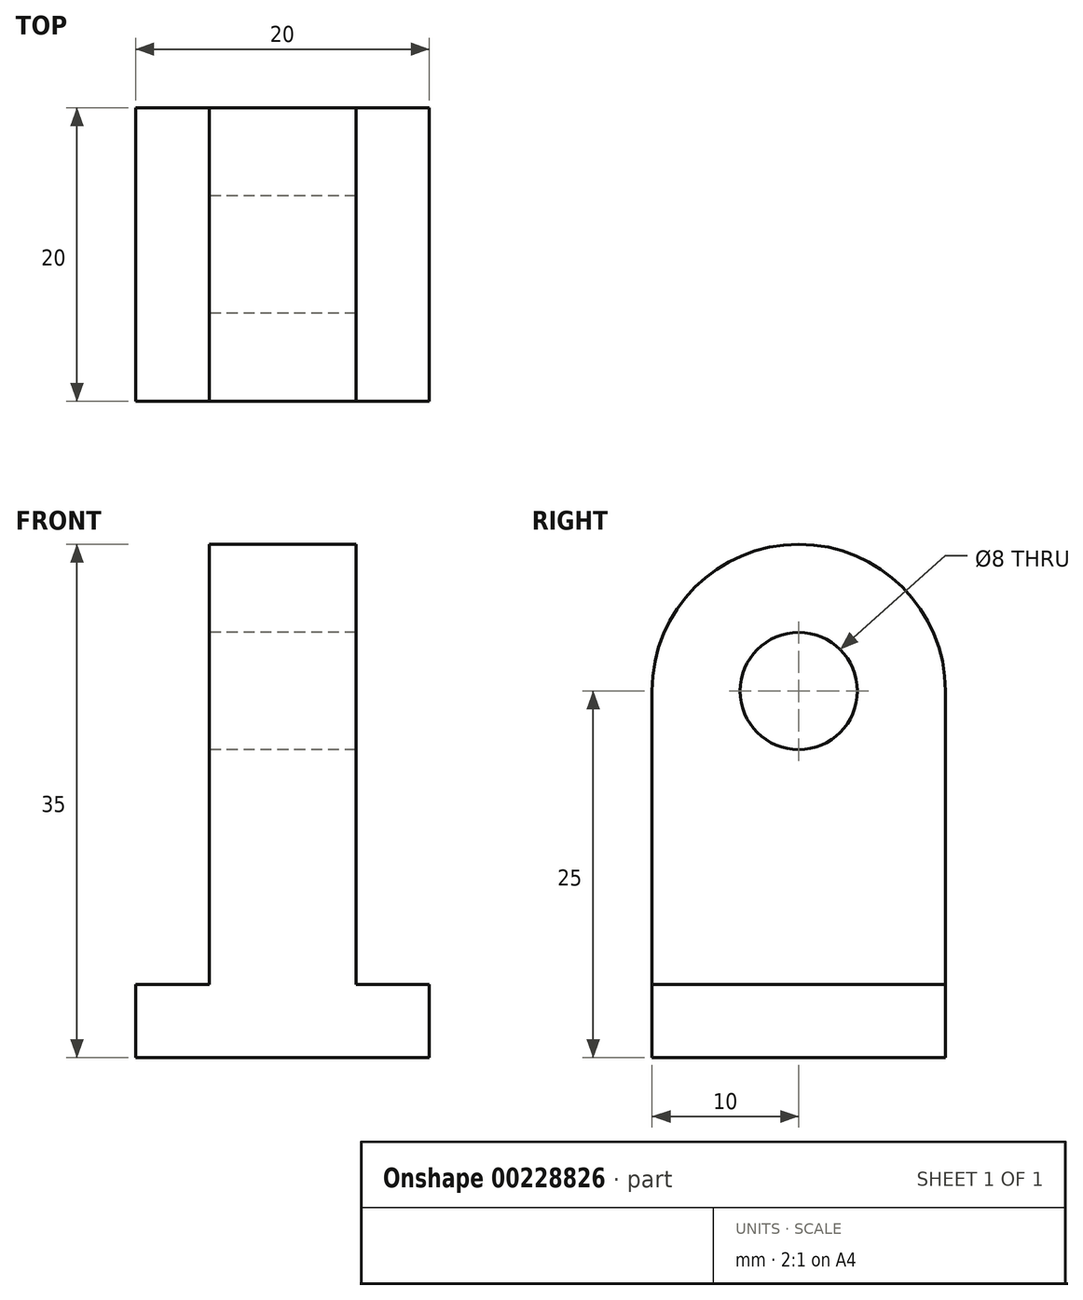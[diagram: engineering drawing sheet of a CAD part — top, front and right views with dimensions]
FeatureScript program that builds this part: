
annotation { "Feature Type Name" : "Feature", "Feature Type Description" : "" }
export const myFeature = defineFeature(function(context is Context, id is Id, definition is map)
    precondition{}
    {
        {
            var Q0;
            Q0=qCreatedBy(makeId("Front.planeOp"),FACE);
            var sketch = newSketch(context, id + "F0", { "sketchPlane" : qUnion([Q0])});
            skLineSegment(sketch, "E0.bottom", {"start": v(-10, 5) * mm, "end": v(10, 5) * mm});
            skLineSegment(sketch, "E0.top", {"start": v(-10, 0) * mm, "end": v(10, 0) * mm});
            skLineSegment(sketch, "E0.left", {"start": v(-10, 5) * mm, "end": v(-10, 0) * mm});
            skLineSegment(sketch, "E0.right", {"start": v(10, 5) * mm, "end": v(10, 0) * mm});
            skLineSegment(sketch, "E1.bottom", {"start": v(-5, 35) * mm, "end": v(5, 35) * mm});
            skLineSegment(sketch, "E1.top", {"start": v(-5, 5) * mm, "end": v(5, 5) * mm});
            skLineSegment(sketch, "E1.left", {"start": v(-5, 35) * mm, "end": v(-5, 5) * mm});
            skLineSegment(sketch, "E1.right", {"start": v(5, 35) * mm, "end": v(5, 5) * mm});
            skSolve(sketch);
        }
        {
            var Q0;
            Q0=makeQuery(id+"F0.imprint","IMPRINT",FACE,{"disambiguationData":[TD([[makeQuery(id+"F0.imprint","IMPRINT",EDGE,{"derivedFrom":sQuery(id+"F0.wireOp",EDGE,"E1.bottom")}),-1.0]])]});
            var Q1;
            Q1=makeQuery(id+"F0.imprint","IMPRINT",FACE,{"disambiguationData":[TD([[makeQuery(id+"F0.imprint","IMPRINT",EDGE,{"derivedFrom":sQuery(id+"F0.wireOp",EDGE,"E0.top")}),1.0]])]});
            extrude(context, id + "F1", {"entities" : qUnion([Q0, Q1]), "depth" : 20 * mm});
        }
        {
            var Q0;
            Q0=makeQuery(id+"F1.opExtrude","CAP_EDGE",EDGE,{"disambiguationData":[OSD([sQuery(id+"F0.wireOp",EDGE,"E1.bottom")])],"isStart":true});
            var Q1;
            Q1=makeQuery(id+"F1.opExtrude","CAP_EDGE",EDGE,{"disambiguationData":[OSD([sQuery(id+"F0.wireOp",EDGE,"E1.bottom")])],"isStart":false});
            fillet(context, id + "F2", {"entities" : qUnion([Q0, Q1]), "radius" : 10 * mm, "tangentPropagation" : true, "allowEdgeOverflow" : false});
        }
        {
            var Q0;
            Q0=makeQuery(id+"F1.opExtrude","SWEPT_FACE",FACE,{"disambiguationData":[OSD([sQuery(id+"F0.wireOp",EDGE,"E1.left")])]});
            var sketch = newSketch(context, id + "F3", { "sketchPlane" : qUnion([Q0])});
            skCircle(sketch, "E2", {"center": v(10, 25) * mm, "radius": 4 * mm});
            skSolve(sketch);
        }
        {
            var Q0;
            Q0 = qSketchRegion(id + "F3", true);
            extrude(context, id + "F4", {"entities" : qUnion([Q0]), "operationType" : NewBodyOperationType.REMOVE, "endBound" : BoundingType.THROUGH_ALL, "oppositeDirection" : true, "depth" : 25 * mm});
        }
    });
